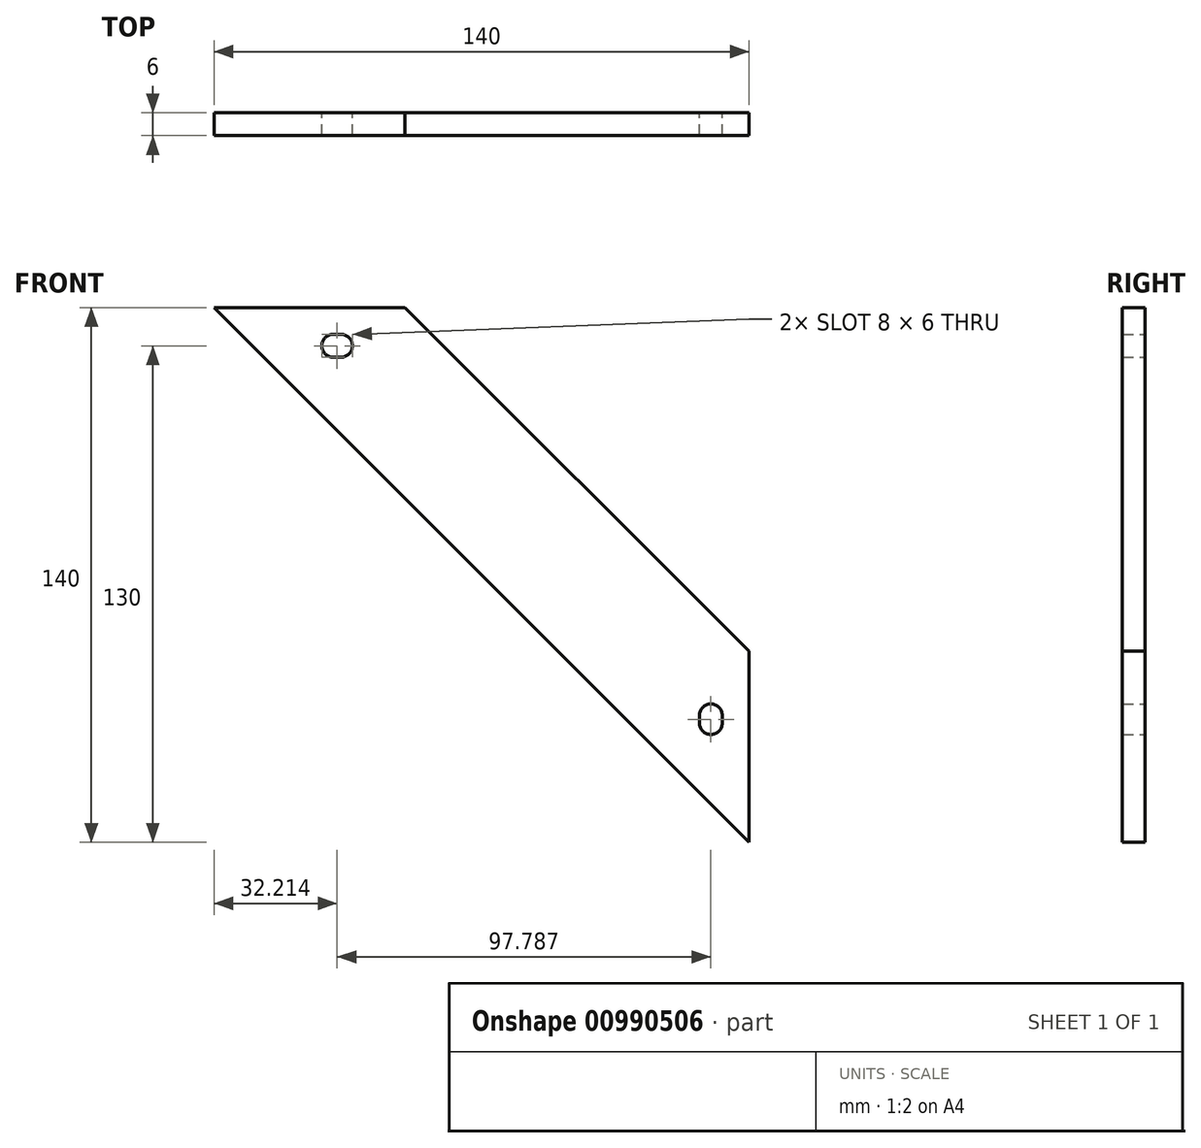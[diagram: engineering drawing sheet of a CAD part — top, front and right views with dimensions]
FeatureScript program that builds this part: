
annotation { "Feature Type Name" : "Feature", "Feature Type Description" : "" }
export const myFeature = defineFeature(function(context is Context, id is Id, definition is map)
    precondition{}
    {
        {
            var Q0;
            Q0=qCreatedBy(makeId("Front.planeOp"),FACE);
            var sketch = newSketch(context, id + "F0", { "sketchPlane" : qUnion([Q0])});
            skLineSegment(sketch, "E0.0.0", {"start": v(65.62, 38.25) * mm, "end": v(65.62, -11.75) * mm});
            skLineSegment(sketch, "E0.0.1", {"start": v(65.62, -11.75) * mm, "end": v(-74.38, 128.25) * mm});
            skLineSegment(sketch, "E0.0.2", {"start": v(-74.38, 128.25) * mm, "end": v(-24.38, 128.25) * mm});
            skLineSegment(sketch, "E0.0.3", {"start": v(-24.38, 128.25) * mm, "end": v(65.62, 38.25) * mm});
            skArc(sketch, "E1.0", {"start": v(-43.17, 115.25) * mm, "mid": v(-46.17, 118.25) * mm, "end": v(-43.17, 121.25) * mm});
            skArc(sketch, "E2.0", {"start": v(-41.17, 121.25) * mm, "mid": v(-38.17, 118.25) * mm, "end": v(-41.17, 115.25) * mm});
            skLineSegment(sketch, "E3.0", {"start": v(-41.17, 115.25) * mm, "end": v(-43.17, 115.25) * mm});
            skLineSegment(sketch, "E4.0", {"start": v(-41.17, 121.25) * mm, "end": v(-43.17, 121.25) * mm});
            skLineSegment(sketch, "E5", {"start": v(20.62, 83.25) * mm, "end": v(-4.38, 58.25) * mm, "construction": true});
            skLineSegment(sketch, "E6.MirrorCS", {"start": v(58.62, 21.46) * mm, "end": v(58.62, 19.46) * mm});
            skArc(sketch, "E7.MirrorCS", {"start": v(58.62, 21.46) * mm, "mid": v(55.62, 24.46) * mm, "end": v(52.62, 21.46) * mm});
            skArc(sketch, "E8.MirrorCS", {"start": v(52.62, 19.46) * mm, "mid": v(55.62, 16.46) * mm, "end": v(58.62, 19.46) * mm});
            skLineSegment(sketch, "E9.MirrorCS", {"start": v(52.62, 21.46) * mm, "end": v(52.62, 19.46) * mm});
            skLineSegment(sketch, "E10", {"start": v(-43.17, 121.25) * mm, "end": v(-43.17, 115.25) * mm, "construction": true});
            skLineSegment(sketch, "E11", {"start": v(-41.17, 121.25) * mm, "end": v(-41.17, 115.25) * mm, "construction": true});
            skSolve(sketch);
        }
        {
            var Q0;
            Q0=makeQuery(id+"F0.imprint","IMPRINT",FACE,{"disambiguationData":[TD([[makeQuery(id+"F0.imprint","IMPRINT",EDGE,{"derivedFrom":sQuery(id+"F0.wireOp",EDGE,"E0.0.0")}),-1.0]])]});
            extrude(context, id + "F1", {"entities" : qUnion([Q0]), "depth" : 6 * mm, "offsetDistance" : 25 * mm});
        }
    });
